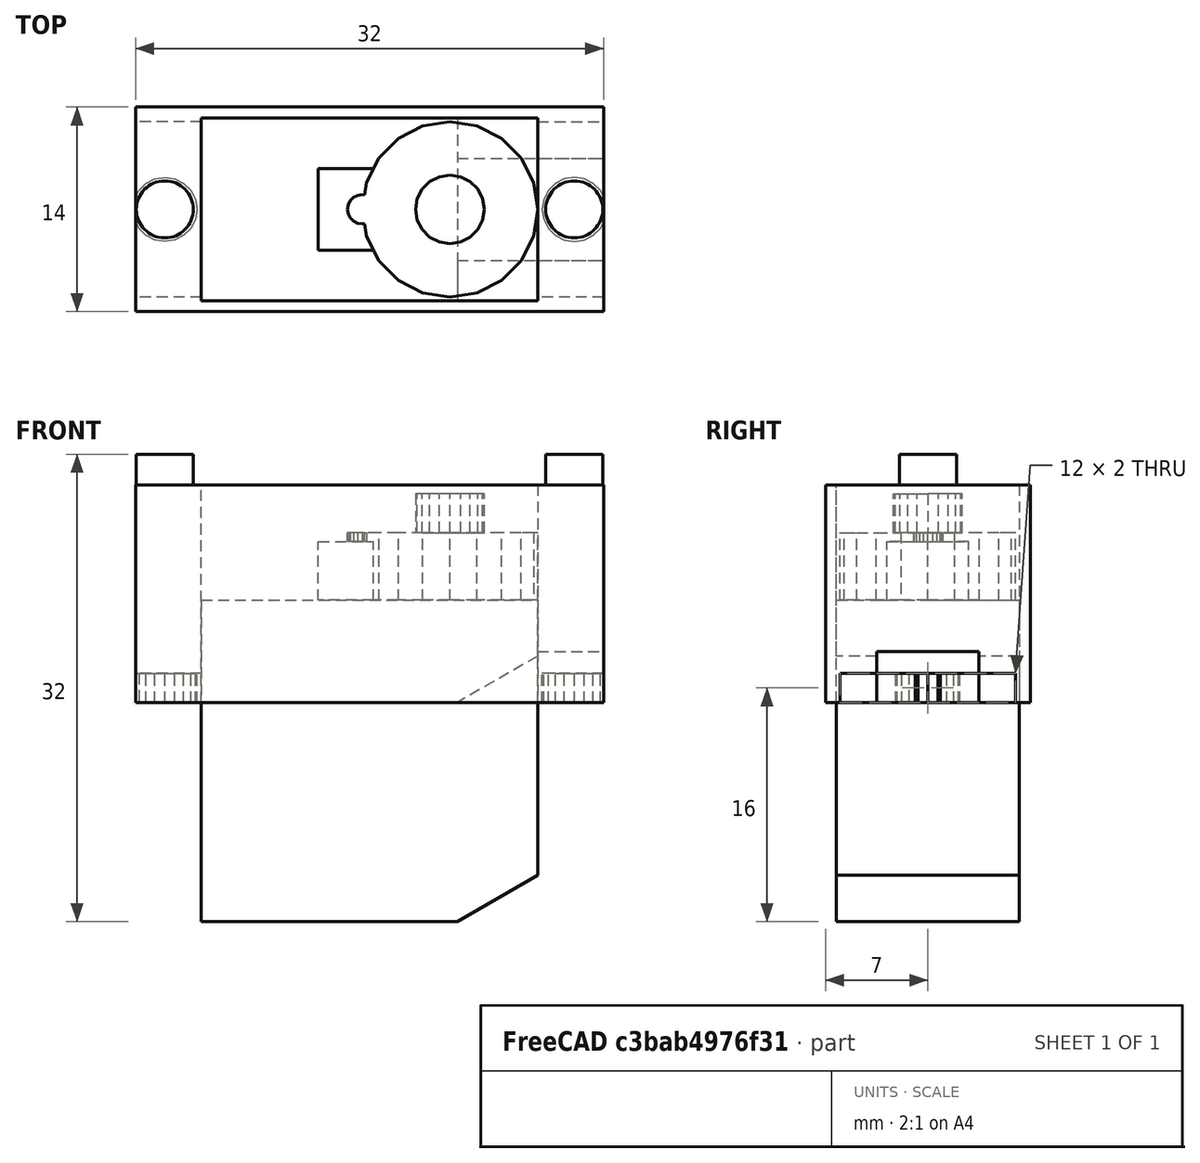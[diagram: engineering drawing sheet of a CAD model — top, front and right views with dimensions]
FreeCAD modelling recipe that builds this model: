
FCSTD DOCUMENT  (FreeCAD 0.21R33771 (Git))
Label: Servo_9g_socket
License: All rights reserved
LicenseURL: https://en.wikipedia.org/wiki/All_rights_reserved
objects: Part::Feature×3, Part::Box×2, Part::Cut×2, Part::Cylinder×2, Part::MultiFuse×1
note: 10 computed .brp shape members not serialized (recipe doc carries the construction recipe); baked Part::Feature solids carry a one-line shape summary decoded from their .brp

FEATURE [Part::Feature] _g_servo002_solid001  label="9g_servo001"
  Placement = pos=(16,7,11) rot=(0,0,1;0rad)
  shape: bbox 32 x 12.5 x 29.27 mm, 117 faces (baked)
FEATURE [Part::Box] Box  label="Cube"
  AttacherType = Attacher::AttachEngine3D
  Height = 14.9
  Length = 32
  Width = 14
FEATURE [Part::Feature] _g_servo002_solid  label="9g_servo"
  Placement = pos=(16,7,-4) rot=(0,0,1;0rad)
  shape: bbox 32 x 12.5 x 29.27 mm, 117 faces (baked)
FEATURE [Part::Cut] Cut
  Base = -> Box
  Tool = -> _g_servo002_solid001
FEATURE [Part::Cylinder] Cylinder  label="Cylindre"
  Angle = 360
  AttacherType = Attacher::AttachEngine3D
  FirstAngle = 0
  Height = 2.1
  Placement = pos=(2,7,14.9) rot=(0,0,1;0rad)
  Radius = 1.95
  SecondAngle = 0
FEATURE [Part::Cylinder] Cylinder001  label="Cylindre001"
  Angle = 360
  AttacherType = Attacher::AttachEngine3D
  FirstAngle = 0
  Height = 2.1
  Placement = pos=(30,7,14.9) rot=(0,0,1;0rad)
  Radius = 1.95
  SecondAngle = 0
FEATURE [Part::MultiFuse] Fusion
  Shapes = -> [Cut,Cylinder,Cylinder001]
FEATURE [Part::Box] Box001  label="Cube001"
  AttacherType = Attacher::AttachEngine3D
  Height = 3.5
  Length = 10
  Placement = pos=(22,3.5,0) rot=(0,0,1;0rad)
  Width = 7
FEATURE [Part::Cut] Cut001
  Base = -> Fusion
  Tool = -> Box001
FEATURE [Part::Feature] _g_servo_arm_single001
  Placement = pos=(158,31,139) rot=(0,0.707107,-0.707107;3.14159rad)
  shape: bbox 6.653 x 4.702 x 19.83 mm, 2412 faces, 0 solids (baked)
